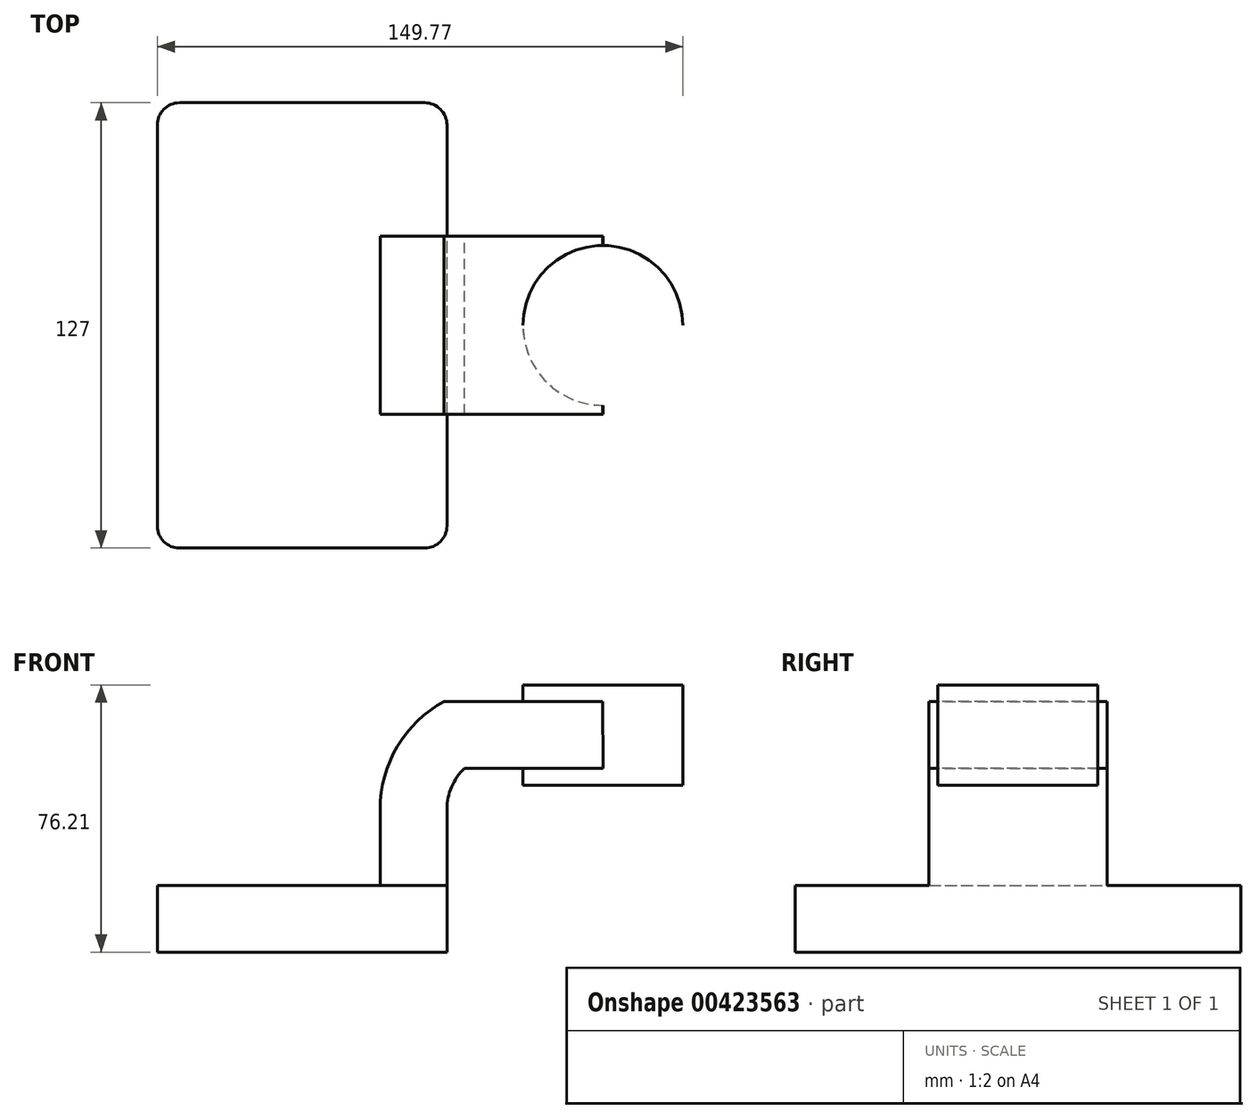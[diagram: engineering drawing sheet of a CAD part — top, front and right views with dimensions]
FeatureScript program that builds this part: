
annotation { "Feature Type Name" : "Feature", "Feature Type Description" : "" }
export const myFeature = defineFeature(function(context is Context, id is Id, definition is map)
    precondition{}
    {
        {
            var Q0;
            Q0=qCreatedBy(makeId("Front.planeOp"),FACE);
            var sketch = newSketch(context, id + "F0", { "sketchPlane" : qUnion([Q0])});
            skLineSegment(sketch, "E0.bottom", {"start": v(41.28, -9.52) * mm, "end": v(-41.28, -9.53) * mm});
            skLineSegment(sketch, "E0.top", {"start": v(41.28, 9.53) * mm, "end": v(-41.28, 9.53) * mm});
            skLineSegment(sketch, "E0.left", {"start": v(41.28, -9.52) * mm, "end": v(41.28, 9.53) * mm});
            skLineSegment(sketch, "E0.right", {"start": v(-41.28, -9.53) * mm, "end": v(-41.28, 9.53) * mm});
            skPoint(sketch, "E0.middle", {"position": v(0, 0) * mm});
            skLineSegment(sketch, "E1.bottom", {"start": v(108.5, 38.1) * mm, "end": v(57.7, 38.1) * mm});
            skLineSegment(sketch, "E1.top", {"start": v(108.5, 66.68) * mm, "end": v(57.7, 66.68) * mm});
            skLineSegment(sketch, "E1.left", {"start": v(108.5, 38.1) * mm, "end": v(108.5, 66.67) * mm});
            skLineSegment(sketch, "E1.right", {"start": v(57.7, 38.1) * mm, "end": v(57.7, 66.67) * mm});
            skPoint(sketch, "E1.middle", {"position": v(83.1, 52.39) * mm});
            skLineSegment(sketch, "E2", {"start": v(41.28, 9.53) * mm, "end": v(41.28, 31.25) * mm});
            skArc(sketch, "E3", {"start": v(41.28, 31.25) * mm, "mid": v(42.6, 37.59) * mm, "end": v(46.34, 42.88) * mm});
            skLineSegment(sketch, "E4", {"start": v(46.34, 42.88) * mm, "end": v(85.72, 42.88) * mm});
            skLineSegment(sketch, "E5.0", {"start": v(40.46, 61.93) * mm, "end": v(85.72, 61.93) * mm});
            skArc(sketch, "E5.1", {"start": v(22.23, 31.25) * mm, "mid": v(27.13, 49.1) * mm, "end": v(40.46, 61.93) * mm});
            skLineSegment(sketch, "E5.2", {"start": v(22.22, 9.53) * mm, "end": v(22.22, 31.25) * mm});
            skFitSpline(sketch, "E6", {"points": [v(-41.28, 9.53) * mm, v(40.46, 61.93) * mm], "startDerivative": vector(9.29, 91.14) * mm, "endDerivative": vector(86.81, -8.87) * mm});
            skLineSegment(sketch, "E7", {"start": v(85.7, 66.68) * mm, "end": v(85.72, 38.1) * mm});
            skSolve(sketch);
        }
        {
            var Q0;
            Q0=makeQuery(id+"F0.imprint","IMPRINT",FACE,{"disambiguationData":[TD([[makeQuery(id+"F0.imprint","IMPRINT",EDGE,{"derivedFrom":sQuery(id+"F0.wireOp",EDGE,"E0.bottom")}),-1.0]])]});
            extrude(context, id + "F1", {"entities" : qUnion([Q0]), "endBound" : BoundingType.SYMMETRIC, "depth" : 127 * mm});
        }
        {
            var Q0;
            {var subQ1=sQuery(id+"F0.wireOp",EDGE,"E2");Q0=makeQuery(id+"F0.imprint","IMPRINT",FACE,{"disambiguationData":[TD([[makeQuery(id+"F0.imprint","IMPRINT",EDGE,{"derivedFrom":subQ1}),1.0]])]});}
            var Q1;
            {var subQ0=sQuery(id+"F0.wireOp",EDGE,"E4");var subQ1=sQuery(id+"F0.wireOp",EDGE,"E1.right");var subQ2=makeQuery(id+"F0.imprint","INTERSECT",VERTEX,{"derivedFrom":[subQ1,subQ0]});Q1=makeQuery(id+"F0.imprint","IMPRINT",FACE,{"disambiguationData":[TD([[makeQuery(id+"F0.imprint","IMPRINT",EDGE,{"disambiguationData":[TD([[subQ2,-1.0]])],"derivedFrom":subQ1}),-1.0]])]});}
            extrude(context, id + "F2", {"entities" : qUnion([Q0, Q1]), "operationType" : NewBodyOperationType.ADD, "endBound" : BoundingType.SYMMETRIC, "depth" : 50.8 * mm});
        }
        {
            var Q0;
            Q0=makeQuery(id+"F0.imprint","IMPRINT",FACE,{"disambiguationData":[TD([[makeQuery(id+"F0.imprint","IMPRINT",EDGE,{"derivedFrom":sQuery(id+"F0.wireOp",EDGE,"E5.1")}),1.0]])]});
            extrude(context, id + "F3", {"entities" : qUnion([Q0]), "operationType" : NewBodyOperationType.ADD, "endBound" : BoundingType.SYMMETRIC, "depth" : 15.88 * mm});
        }
        {
            var Q0;
            {var subQ0=sQuery(id+"F0.wireOp",EDGE,"E1.left");Q0=makeQuery(id+"F0.imprint","IMPRINT",FACE,{"disambiguationData":[TD([[makeQuery(id+"F0.imprint","IMPRINT",EDGE,{"derivedFrom":subQ0}),1.0]])]});}
            var Q1;
            Q1=sQuery(id+"F0.wireOp",EDGE,"E7");
            revolve(context, id + "F4", {"operationType" : NewBodyOperationType.ADD, "entities" : qUnion([Q0]), "axis" : qUnion([Q1]), "revolveType" : RevolveType.FULL});
        }
        {
            var Q0;
            Q0=makeQuery(id+"F1.opExtrude","CAP_EDGE",EDGE,{"disambiguationData":[OSD([sQuery(id+"F0.wireOp",EDGE,"E0.left")])],"isStart":false});
            var Q1;
            Q1=makeQuery(id+"F1.opExtrude","CAP_EDGE",EDGE,{"disambiguationData":[OSD([sQuery(id+"F0.wireOp",EDGE,"E0.right")])],"isStart":false});
            var Q2;
            Q2=makeQuery(id+"F1.opExtrude","CAP_EDGE",EDGE,{"disambiguationData":[OSD([sQuery(id+"F0.wireOp",EDGE,"E0.right")])],"isStart":true});
            var Q3;
            Q3=makeQuery(id+"F1.opExtrude","CAP_EDGE",EDGE,{"disambiguationData":[OSD([sQuery(id+"F0.wireOp",EDGE,"E0.left")])],"isStart":true});
            fillet(context, id + "F5", {"entities" : qUnion([Q0, Q1, Q2, Q3]), "radius" : 6.35 * mm, "tangentPropagation" : true, "allowEdgeOverflow" : false});
        }
    });
